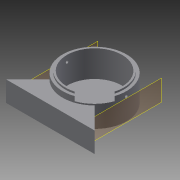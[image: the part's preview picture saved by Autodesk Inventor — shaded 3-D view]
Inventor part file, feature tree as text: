
AUTODESK INVENTOR PART (.ipt)
format: ipt  version: 2015 SP2 (Build 190223200, 223)  size: 149,504 bytes
history: native  units: in
note: dims shown in document units (in); Inventor stores cm internally (conversion verified against a paired STEP export)
features: sketch x7, extrude x5, plane x2, hole x2, projected_geometry x2
ambient origin geometry x8: Origin, YZ Plane, XZ Plane, XY Plane, X Axis, Y Axis, Z Axis, Center Point
bodies: Solid1 (feature_tree)
feature tree (18):
  extrude  "Extrusion1"  Depth=0.0591in TaperAngle=0.0deg
  extrude  "Extrusion2"  Depth=0.0787in
  extrude  "Extrusion3"  Depth=1.1024in TaperAngle=0.0deg
  extrude  "Extrusion4"  TaperAngle=45.0deg  [1 undecoded]
  plane  "Work Plane1"
  hole  "Hole1"  [1 undecoded]
  plane  "Work Plane2"
  hole  "Hole2"  [1 undecoded]
  extrude  "Extrusion5"  Depth=0.0591in
  sketch  "Sketch1"  dims[d0=2.8346in d1=0.0591in d2=0.0in]
  sketch  "Sketch2"  dims[d3=0.1181in d4=0.0787in]
  projected_geometry  "Projected Loop1"
  sketch  "Sketch3"  dims[d5=1.1811in d6=0.0in d7=1.1024in d8=0.0in]
  projected_geometry  "Projected Loop2"
  sketch  "Sketch5"  dims[d13=1.7717in d16=0.2756in d17=0.0in d18=45.0deg]
  sketch  "Sketch7"  dims[d19=45.0deg d23=2.8346in]
  sketch  "Sketch8"  dims[d24=2.5984in d25=2.4409in]
  sketch  "Sketch10"  dims[d26=0.1181in d27=0.1969in d28=0.1181in d29=0.2362in d30=0.1575in d31=0.0787in d32=90.0deg d33=0.315in d34=0.8108in d35=0.1181in d36=0.2362in d37=0.1575in d38=0.0787in d39=90.0deg d40=0.315in d41=0.8108in d42=0.1181in d43=0.1969in d44=1.9685in d45=45.0deg d46=135.0deg d47=0.8465in d48=0.0in d49=0.0591in d50=0.0in d51=2.8346in d52=2.5984in]
note: 3 required parameter values undecoded (feature->parameter linkage not recoverable at this tier; creation-order binding heuristic only, values carry confidence <= 0.55)
